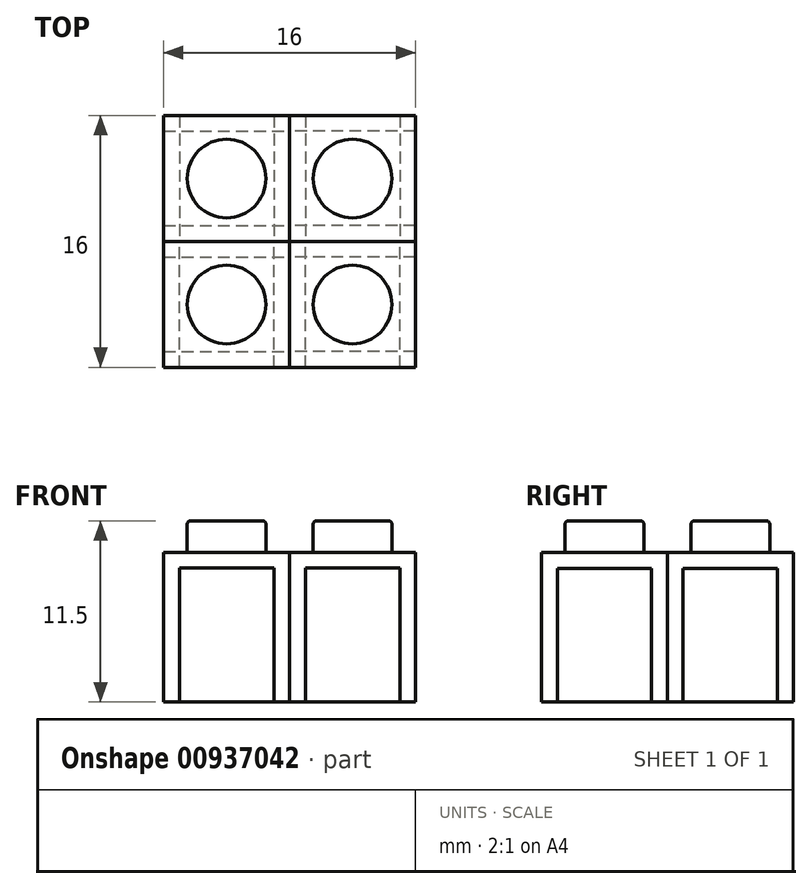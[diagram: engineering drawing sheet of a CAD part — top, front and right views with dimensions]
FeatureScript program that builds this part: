
annotation { "Feature Type Name" : "Feature", "Feature Type Description" : "" }
export const myFeature = defineFeature(function(context is Context, id is Id, definition is map)
    precondition{}
    {
        {
            var Q0;
            Q0=qCreatedBy(makeId("Front.planeOp"),FACE);
            var sketch = newSketch(context, id + "F0", { "sketchPlane" : qUnion([Q0])});
            skLineSegment(sketch, "E0.bottom", {"start": v(0, 4.75) * mm, "end": v(-4, 4.75) * mm});
            skPoint(sketch, "E0.middle", {"position": v(0, 0) * mm});
            skLineSegment(sketch, "E1.bottom", {"start": v(-2.5, 6.75) * mm, "end": v(0, 6.75) * mm});
            skLineSegment(sketch, "E1.top", {"start": v(-2.5, 4.75) * mm, "end": v(0, 4.75) * mm});
            skLineSegment(sketch, "E1.left", {"start": v(-2.5, 6.75) * mm, "end": v(-2.5, 4.75) * mm});
            skLineSegment(sketch, "E1.right", {"start": v(0, 6.75) * mm, "end": v(0, 4.75) * mm});
            skLineSegment(sketch, "E2", {"start": v(-4, 4.75) * mm, "end": v(-4, -4.75) * mm});
            skPoint(sketch, "E3.orphan", {"position": v(4, 4.75) * mm});
            skLineSegment(sketch, "E4", {"start": v(-4, -4.75) * mm, "end": v(-3, -4.75) * mm});
            skLineSegment(sketch, "E5", {"start": v(-3, 3.75) * mm, "end": v(0, 3.75) * mm});
            skLineSegment(sketch, "E6", {"start": v(0, 3.75) * mm, "end": v(0, 4.75) * mm});
            skLineSegment(sketch, "E7", {"start": v(-3, 3.75) * mm, "end": v(-3, -4.75) * mm});
            skLineSegment(sketch, "E8", {"start": v(0, 4.75) * mm, "end": v(4, 4.75) * mm});
            skLineSegment(sketch, "E9", {"start": v(0, 3.75) * mm, "end": v(3, 3.75) * mm});
            skLineSegment(sketch, "E10", {"start": v(3, 3.75) * mm, "end": v(3, -4.75) * mm});
            skLineSegment(sketch, "E11", {"start": v(3, -4.75) * mm, "end": v(4, -4.75) * mm});
            skLineSegment(sketch, "E12", {"start": v(4, -4.75) * mm, "end": v(4, 4.75) * mm});
            skSolve(sketch);
        }
        {
            var Q0;
            Q0=makeQuery(id+"F0.imprint","IMPRINT",FACE,{"disambiguationData":[TD([[makeQuery(id+"F0.imprint","IMPRINT",EDGE,{"derivedFrom":sQuery(id+"F0.wireOp",EDGE,"E1.bottom")}),-1.0]])]});
            var Q1;
            Q1=sQuery(id+"F0.wireOp",EDGE,"E1.right");
            revolve(context, id + "F1", {"surfaceOperationType" : NewSurfaceOperationType.NEW, "entities" : qUnion([Q0]), "axis" : qUnion([Q1]), "revolveType" : RevolveType.FULL});
        }
        {
            var Q0;
            Q0=makeQuery(id+"F1.opRevolve","SWEPT_EDGE",EDGE,{"disambiguationData":[OSD([sQuery(id+"F0.wireOp",EDGE,"E1.bottom"),sQuery(id+"F0.wireOp",EDGE,"E1.left")])]});
            fillet(context, id + "F2", {"entities" : qUnion([Q0]), "radius" : 0.2 * mm, "tangentPropagation" : true, "allowEdgeOverflow" : false});
        }
        {
            var Q0;
            Q0=qCreatedBy(makeId("Right.planeOp"),FACE);
            var sketch = newSketch(context, id + "F3", { "sketchPlane" : qUnion([Q0])});
            skLineSegment(sketch, "E13.bottom", {"start": v(4, 4.75) * mm, "end": v(-4, 4.75) * mm});
            skLineSegment(sketch, "E13.left", {"start": v(4, 4.75) * mm, "end": v(4, -4.75) * mm});
            skLineSegment(sketch, "E13.right", {"start": v(-4, 4.75) * mm, "end": v(-4, -4.75) * mm});
            skPoint(sketch, "E13.middle", {"position": v(0, 0) * mm});
            skLineSegment(sketch, "E14", {"start": v(-4, -4.75) * mm, "end": v(-3, -4.75) * mm});
            skLineSegment(sketch, "E15", {"start": v(-3, -4.75) * mm, "end": v(-3, 3.75) * mm});
            skLineSegment(sketch, "E16", {"start": v(-3, 3.75) * mm, "end": v(0, 3.75) * mm});
            skLineSegment(sketch, "E17", {"start": v(0, 3.75) * mm, "end": v(3, 3.75) * mm});
            skLineSegment(sketch, "E18", {"start": v(3, 3.75) * mm, "end": v(3, -4.75) * mm});
            skLineSegment(sketch, "E19", {"start": v(3, -4.75) * mm, "end": v(4, -4.75) * mm});
            skSolve(sketch);
        }
        {
            var Q0;
            Q0 = qSketchRegion(id + "F3", true);
            extrude(context, id + "F4", {"entities" : qUnion([Q0]), "depth" : 8 * mm, "offsetDistance" : 25.4 * mm, "symmetric" : true});
        }
        {
            var Q0;
            {var subQ0=sQuery(id+"F0.wireOp",EDGE,"E2");Q0=makeQuery(id+"F0.imprint","IMPRINT",FACE,{"disambiguationData":[TD([[makeQuery(id+"F0.imprint","IMPRINT",EDGE,{"derivedFrom":subQ0}),1.0]])]});}
            var Q1;
            Q1=makeQuery(id+"F0.imprint","IMPRINT",FACE,{"disambiguationData":[TD([[makeQuery(id+"F0.imprint","IMPRINT",EDGE,{"derivedFrom":sQuery(id+"F0.wireOp",EDGE,"E6")}),-1.0]])]});
            extrude(context, id + "F5", {"entities" : qUnion([Q0, Q1]), "depth" : 8 * mm, "offsetDistance" : 25.4 * mm, "symmetric" : true});
        }
        {
            var Q0;
            Q0=makeQuery(id+"F1.opRevolve","SWEPT_BODY",BODY,{"disambiguationData":[OSD([sQuery(id+"F0.wireOp",EDGE,"E0.bottom"),sQuery(id+"F0.wireOp",EDGE,"E1.bottom"),sQuery(id+"F0.wireOp",EDGE,"E1.left"),sQuery(id+"F0.wireOp",EDGE,"E1.right")])]});
            var Q1;
            Q1=makeQuery(id+"F5.opExtrude","SWEPT_BODY",BODY,{"disambiguationData":[OSD([sQuery(id+"F0.wireOp",EDGE,"E0.bottom"),sQuery(id+"F0.wireOp",EDGE,"E2"),sQuery(id+"F0.wireOp",EDGE,"E4"),sQuery(id+"F0.wireOp",EDGE,"E5"),sQuery(id+"F0.wireOp",EDGE,"E7"),sQuery(id+"F0.wireOp",EDGE,"E8"),sQuery(id+"F0.wireOp",EDGE,"E9"),sQuery(id+"F0.wireOp",EDGE,"E10"),sQuery(id+"F0.wireOp",EDGE,"E11"),sQuery(id+"F0.wireOp",EDGE,"E12")])]});
            var Q2;
            Q2=makeQuery(id+"F4.opExtrude","SWEPT_BODY",BODY,{"disambiguationData":[OSD([sQuery(id+"F3.wireOp",EDGE,"E13.bottom"),sQuery(id+"F3.wireOp",EDGE,"E13.left"),sQuery(id+"F3.wireOp",EDGE,"E13.right"),sQuery(id+"F3.wireOp",EDGE,"E14"),sQuery(id+"F3.wireOp",EDGE,"E15"),sQuery(id+"F3.wireOp",EDGE,"E16"),sQuery(id+"F3.wireOp",EDGE,"E17"),sQuery(id+"F3.wireOp",EDGE,"E18"),sQuery(id+"F3.wireOp",EDGE,"E19")])]});
            var Q3;
            Q3=makeQuery(id+"F5.opExtrude","SWEPT_FACE",FACE,{"disambiguationData":[OSD([sQuery(id+"F0.wireOp",EDGE,"E2")])]});
            mirror(context, id + "F6", {"entities" : qUnion([Q0, Q1, Q2]), "mirrorPlane" : qUnion([Q3])});
        }
        {
            var Q0;
            Q0=makeQuery(id+"F1.opRevolve","SWEPT_BODY",BODY,{"disambiguationData":[OSD([sQuery(id+"F0.wireOp",EDGE,"E0.bottom"),sQuery(id+"F0.wireOp",EDGE,"E1.bottom"),sQuery(id+"F0.wireOp",EDGE,"E1.left"),sQuery(id+"F0.wireOp",EDGE,"E1.right")])]});
            var Q1;
            Q1=makeQuery(id+"F4.opExtrude","SWEPT_BODY",BODY,{"disambiguationData":[OSD([sQuery(id+"F3.wireOp",EDGE,"E13.bottom"),sQuery(id+"F3.wireOp",EDGE,"E13.left"),sQuery(id+"F3.wireOp",EDGE,"E13.right"),sQuery(id+"F3.wireOp",EDGE,"E14"),sQuery(id+"F3.wireOp",EDGE,"E15"),sQuery(id+"F3.wireOp",EDGE,"E16"),sQuery(id+"F3.wireOp",EDGE,"E17"),sQuery(id+"F3.wireOp",EDGE,"E18"),sQuery(id+"F3.wireOp",EDGE,"E19")])]});
            var Q2;
            Q2=makeQuery(id+"F5.opExtrude","SWEPT_BODY",BODY,{"disambiguationData":[OSD([sQuery(id+"F0.wireOp",EDGE,"E0.bottom"),sQuery(id+"F0.wireOp",EDGE,"E2"),sQuery(id+"F0.wireOp",EDGE,"E4"),sQuery(id+"F0.wireOp",EDGE,"E5"),sQuery(id+"F0.wireOp",EDGE,"E7"),sQuery(id+"F0.wireOp",EDGE,"E8"),sQuery(id+"F0.wireOp",EDGE,"E9"),sQuery(id+"F0.wireOp",EDGE,"E10"),sQuery(id+"F0.wireOp",EDGE,"E11"),sQuery(id+"F0.wireOp",EDGE,"E12")])]});
            var Q3;
            Q3=makeQuery(id+"F6.opPattern","COPY",BODY,{"derivedFrom":makeQuery(id+"F1.opRevolve","SWEPT_BODY",BODY,{"disambiguationData":[OSD([sQuery(id+"F0.wireOp",EDGE,"E0.bottom"),sQuery(id+"F0.wireOp",EDGE,"E1.bottom"),sQuery(id+"F0.wireOp",EDGE,"E1.left"),sQuery(id+"F0.wireOp",EDGE,"E1.right")])]}),"instanceName":"1"});
            var Q4;
            Q4=makeQuery(id+"F6.opPattern","COPY",BODY,{"derivedFrom":makeQuery(id+"F4.opExtrude","SWEPT_BODY",BODY,{"disambiguationData":[OSD([sQuery(id+"F3.wireOp",EDGE,"E13.bottom"),sQuery(id+"F3.wireOp",EDGE,"E13.left"),sQuery(id+"F3.wireOp",EDGE,"E13.right"),sQuery(id+"F3.wireOp",EDGE,"E14"),sQuery(id+"F3.wireOp",EDGE,"E15"),sQuery(id+"F3.wireOp",EDGE,"E16"),sQuery(id+"F3.wireOp",EDGE,"E17"),sQuery(id+"F3.wireOp",EDGE,"E18"),sQuery(id+"F3.wireOp",EDGE,"E19")])]}),"instanceName":"1"});
            var Q5;
            Q5=makeQuery(id+"F6.opPattern","COPY",BODY,{"derivedFrom":makeQuery(id+"F5.opExtrude","SWEPT_BODY",BODY,{"disambiguationData":[OSD([sQuery(id+"F0.wireOp",EDGE,"E0.bottom"),sQuery(id+"F0.wireOp",EDGE,"E2"),sQuery(id+"F0.wireOp",EDGE,"E4"),sQuery(id+"F0.wireOp",EDGE,"E5"),sQuery(id+"F0.wireOp",EDGE,"E7"),sQuery(id+"F0.wireOp",EDGE,"E8"),sQuery(id+"F0.wireOp",EDGE,"E9"),sQuery(id+"F0.wireOp",EDGE,"E10"),sQuery(id+"F0.wireOp",EDGE,"E11"),sQuery(id+"F0.wireOp",EDGE,"E12")])]}),"instanceName":"1"});
            var Q6;
            Q6=makeQuery(id+"F6.opPattern","COPY",FACE,{"derivedFrom":makeQuery(id+"F4.opExtrude","SWEPT_FACE",FACE,{"disambiguationData":[OSD([sQuery(id+"F3.wireOp",EDGE,"E13.left")])]}),"instanceName":"1"});
            mirror(context, id + "F7", {"entities" : qUnion([Q0, Q1, Q2, Q3, Q4, Q5]), "mirrorPlane" : qUnion([Q6])});
        }
    });
